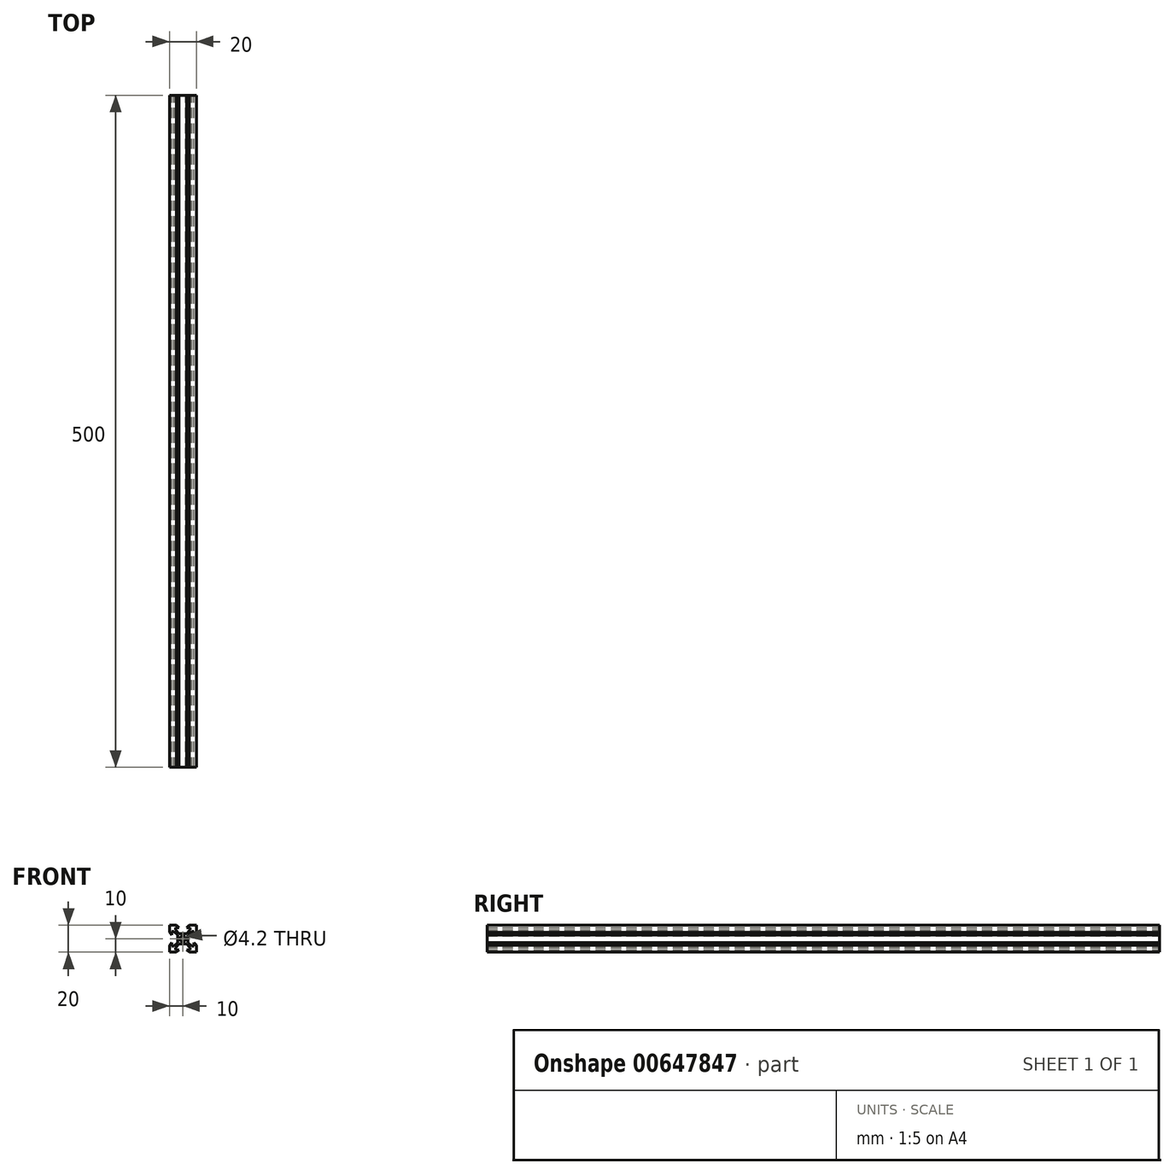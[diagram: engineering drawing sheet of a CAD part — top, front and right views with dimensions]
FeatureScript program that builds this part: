
annotation { "Feature Type Name" : "Feature", "Feature Type Description" : "" }
export const myFeature = defineFeature(function(context is Context, id is Id, definition is map)
    precondition{}
    {
        {
            var Q0;
            Q0=qCreatedBy(makeId("Front.planeOp"),FACE);
            var sketch = newSketch(context, id + "F0", { "sketchPlane" : qUnion([Q0])});
            skLineSegment(sketch, "E0.bottom", {"start": v(-3.9, -3.9) * mm, "end": v(3.9, -3.9) * mm});
            skLineSegment(sketch, "E0.top", {"start": v(-3.9, 3.9) * mm, "end": v(3.9, 3.9) * mm});
            skLineSegment(sketch, "E0.left", {"start": v(-3.9, -3.9) * mm, "end": v(-3.9, 3.9) * mm});
            skLineSegment(sketch, "E0.right", {"start": v(3.9, -3.9) * mm, "end": v(3.9, 3.9) * mm});
            skPoint(sketch, "E1", {"position": v(0, 3.9) * mm});
            skPoint(sketch, "E2", {"position": v(-3.9, 0) * mm});
            skLineSegment(sketch, "E3", {"start": v(0, 0) * mm, "end": v(-11.86, 11.86) * mm, "construction": true});
            skLineSegment(sketch, "E4", {"start": v(-10, 10) * mm, "end": v(-10, 4.64) * mm});
            skLineSegment(sketch, "E5", {"start": v(-10, 4.64) * mm, "end": v(-8.2, 2.84) * mm});
            skLineSegment(sketch, "E6", {"start": v(-8.2, 2.84) * mm, "end": v(-8.2, 5.5) * mm});
            skLineSegment(sketch, "E7", {"start": v(-8.2, 5.5) * mm, "end": v(-6.56, 5.5) * mm});
            skLineSegment(sketch, "E8", {"start": v(-6.56, 5.5) * mm, "end": v(-3.9, 2.84) * mm});
            skLineSegment(sketch, "E9", {"start": v(-10, 10) * mm, "end": v(-4.64, 10) * mm});
            skLineSegment(sketch, "E10", {"start": v(-4.64, 10) * mm, "end": v(-2.84, 8.2) * mm});
            skLineSegment(sketch, "E11", {"start": v(-2.84, 8.2) * mm, "end": v(-5.5, 8.2) * mm});
            skLineSegment(sketch, "E12", {"start": v(-5.5, 8.2) * mm, "end": v(-5.5, 6.56) * mm});
            skLineSegment(sketch, "E13", {"start": v(-5.5, 6.56) * mm, "end": v(-2.84, 3.9) * mm});
            skLineSegment(sketch, "E14.1.0", {"start": v(-6.56, -5.5) * mm, "end": v(-3.9, -2.84) * mm});
            skLineSegment(sketch, "E14.1.1", {"start": v(-8.2, -5.5) * mm, "end": v(-6.56, -5.5) * mm});
            skLineSegment(sketch, "E14.1.2", {"start": v(-5.5, -6.56) * mm, "end": v(-2.84, -3.9) * mm});
            skLineSegment(sketch, "E14.1.3", {"start": v(-10, -10) * mm, "end": v(-10, -4.64) * mm});
            skLineSegment(sketch, "E14.1.4", {"start": v(-5.5, -8.2) * mm, "end": v(-5.5, -6.56) * mm});
            skLineSegment(sketch, "E14.1.5", {"start": v(-10, -10) * mm, "end": v(-4.64, -10) * mm});
            skLineSegment(sketch, "E14.1.6", {"start": v(-4.64, -10) * mm, "end": v(-2.84, -8.2) * mm});
            skLineSegment(sketch, "E14.1.7", {"start": v(-2.84, -8.2) * mm, "end": v(-5.5, -8.2) * mm});
            skLineSegment(sketch, "E14.1.8", {"start": v(-10, -4.64) * mm, "end": v(-8.2, -2.84) * mm});
            skLineSegment(sketch, "E14.1.9", {"start": v(-8.2, -2.84) * mm, "end": v(-8.2, -5.5) * mm});
            skLineSegment(sketch, "E14.2.0", {"start": v(5.5, -6.56) * mm, "end": v(2.84, -3.9) * mm});
            skLineSegment(sketch, "E14.2.1", {"start": v(5.5, -8.2) * mm, "end": v(5.5, -6.56) * mm});
            skLineSegment(sketch, "E14.2.2", {"start": v(6.56, -5.5) * mm, "end": v(3.9, -2.84) * mm});
            skLineSegment(sketch, "E14.2.3", {"start": v(10, -10) * mm, "end": v(4.64, -10) * mm});
            skLineSegment(sketch, "E14.2.4", {"start": v(8.2, -5.5) * mm, "end": v(6.56, -5.5) * mm});
            skLineSegment(sketch, "E14.2.5", {"start": v(10, -10) * mm, "end": v(10, -4.64) * mm});
            skLineSegment(sketch, "E14.2.6", {"start": v(10, -4.64) * mm, "end": v(8.2, -2.84) * mm});
            skLineSegment(sketch, "E14.2.7", {"start": v(8.2, -2.84) * mm, "end": v(8.2, -5.5) * mm});
            skLineSegment(sketch, "E14.2.8", {"start": v(4.64, -10) * mm, "end": v(2.84, -8.2) * mm});
            skLineSegment(sketch, "E14.2.9", {"start": v(2.84, -8.2) * mm, "end": v(5.5, -8.2) * mm});
            skLineSegment(sketch, "E14.3.0", {"start": v(6.56, 5.5) * mm, "end": v(3.9, 2.84) * mm});
            skLineSegment(sketch, "E14.3.1", {"start": v(8.2, 5.5) * mm, "end": v(6.56, 5.5) * mm});
            skLineSegment(sketch, "E14.3.2", {"start": v(5.5, 6.56) * mm, "end": v(2.84, 3.9) * mm});
            skLineSegment(sketch, "E14.3.3", {"start": v(10, 10) * mm, "end": v(10, 4.64) * mm});
            skLineSegment(sketch, "E14.3.4", {"start": v(5.5, 8.2) * mm, "end": v(5.5, 6.56) * mm});
            skLineSegment(sketch, "E14.3.5", {"start": v(10, 10) * mm, "end": v(4.64, 10) * mm});
            skLineSegment(sketch, "E14.3.6", {"start": v(4.64, 10) * mm, "end": v(2.84, 8.2) * mm});
            skLineSegment(sketch, "E14.3.7", {"start": v(2.84, 8.2) * mm, "end": v(5.5, 8.2) * mm});
            skLineSegment(sketch, "E14.3.8", {"start": v(10, 4.64) * mm, "end": v(8.2, 2.84) * mm});
            skLineSegment(sketch, "E14.3.9", {"start": v(8.2, 2.84) * mm, "end": v(8.2, 5.5) * mm});
            skPoint(sketch, "E14.center", {"position": v(0, 0) * mm});
            skCircle(sketch, "E15", {"center": v(0, 0) * mm, "radius": 2.1 * mm});
            skSolve(sketch);
        }
        {
            var Q0;
            Q0=makeQuery(id+"F0.imprint","IMPRINT",FACE,{"disambiguationData":[TD([[makeQuery(id+"F0.imprint","IMPRINT",EDGE,{"derivedFrom":sQuery(id+"F0.wireOp",EDGE,"E4")}),1.0]])]});
            var Q1;
            Q1=makeQuery(id+"F0.imprint","IMPRINT",FACE,{"disambiguationData":[TD([[makeQuery(id+"F0.imprint","IMPRINT",EDGE,{"derivedFrom":sQuery(id+"F0.wireOp",EDGE,"E15")}),-1.0]])]});
            var Q2;
            {var subQ3=sQuery(id+"F0.wireOp",EDGE,"E14.1.0");Q2=makeQuery(id+"F0.imprint","IMPRINT",FACE,{"disambiguationData":[TD([[makeQuery(id+"F0.imprint","IMPRINT",EDGE,{"derivedFrom":subQ3}),-1.0]])]});}
            var Q3;
            {var subQ4=sQuery(id+"F0.wireOp",EDGE,"E14.2.0");Q3=makeQuery(id+"F0.imprint","IMPRINT",FACE,{"disambiguationData":[TD([[makeQuery(id+"F0.imprint","IMPRINT",EDGE,{"derivedFrom":subQ4}),-1.0]])]});}
            var Q4;
            {var subQ4=sQuery(id+"F0.wireOp",EDGE,"E14.3.0");Q4=makeQuery(id+"F0.imprint","IMPRINT",FACE,{"disambiguationData":[TD([[makeQuery(id+"F0.imprint","IMPRINT",EDGE,{"derivedFrom":subQ4}),-1.0]])]});}
            extrude(context, id + "F1", {"entities" : qUnion([Q0, Q1, Q2, Q3, Q4]), "endBound" : BoundingType.SYMMETRIC, "depth" : 500 * mm, "offsetDistance" : 25.4 * mm});
        }
    });
